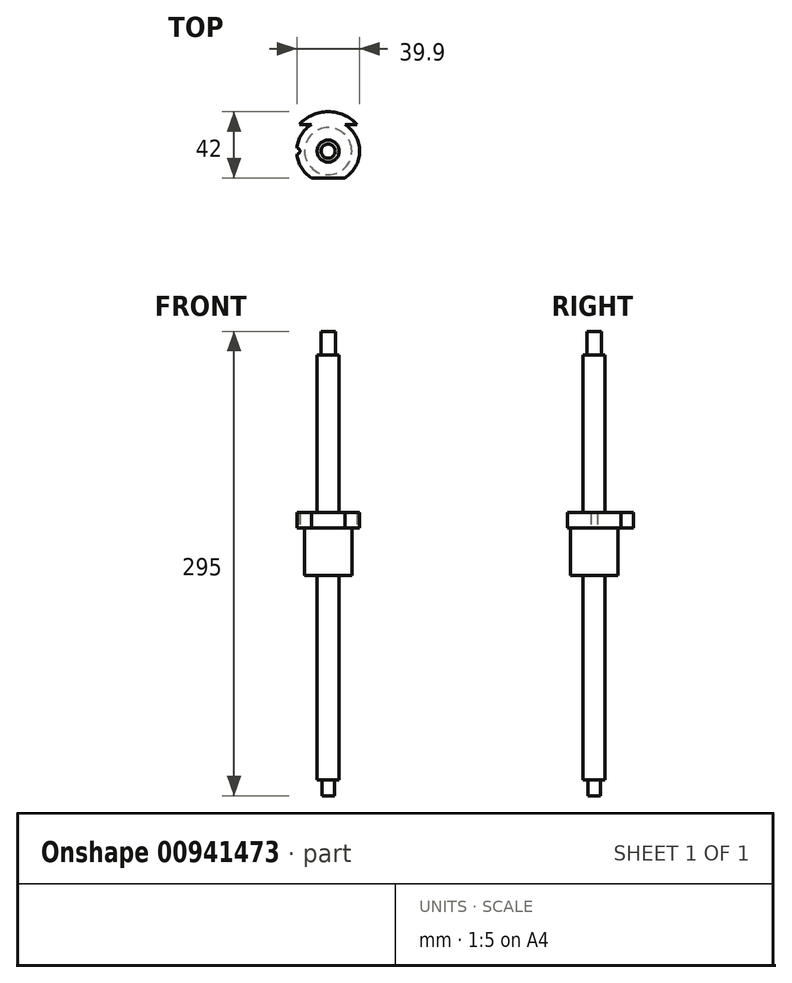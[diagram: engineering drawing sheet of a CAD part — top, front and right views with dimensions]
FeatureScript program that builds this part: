
annotation { "Feature Type Name" : "Feature", "Feature Type Description" : "" }
export const myFeature = defineFeature(function(context is Context, id is Id, definition is map)
    precondition{}
    {
        {
            var Q0;
            Q0=qCreatedBy(makeId("Top.planeOp"),FACE);
            var sketch = newSketch(context, id + "F0", { "sketchPlane" : qUnion([Q0])});
            skCircle(sketch, "E0", {"center": v(0, 0) * mm, "radius": 15 * mm});
            skSolve(sketch);
        }
        {
            var Q0;
            Q0=makeQuery(id+"F0.imprint","IMPRINT",FACE,{"disambiguationData":[TD([[makeQuery(id+"F0.imprint","IMPRINT",EDGE,{"derivedFrom":sQuery(id+"F0.wireOp",EDGE,"E0")}),1.0]])]});
            extrude(context, id + "F1", {"entities" : qUnion([Q0]), "depth" : 30 * mm, "offsetDistance" : 25 * mm});
        }
        {
            var Q0;
            Q0=makeQuery(id+"F1.opExtrude","CAP_FACE",FACE,{"disambiguationData":[OSD([sQuery(id+"F0.wireOp",EDGE,"E0")])],"isStart":false});
            var sketch = newSketch(context, id + "F2", { "sketchPlane" : qUnion([Q0])});
            skCircle(sketch, "E1", {"center": v(0, 0) * mm, "radius": 20 * mm});
            skCircle(sketch, "E2", {"center": v(0, 0) * mm, "radius": 25 * mm});
            skLineSegment(sketch, "E3.bottom", {"start": v(30.85, -17) * mm, "end": v(-30.85, -17) * mm});
            skLineSegment(sketch, "E3.top", {"start": v(30.85, 17) * mm, "end": v(-30.85, 17) * mm});
            skLineSegment(sketch, "E3.left", {"start": v(30.85, -17) * mm, "end": v(30.85, 17) * mm});
            skLineSegment(sketch, "E3.right", {"start": v(-30.85, -17) * mm, "end": v(-30.85, 17) * mm});
            skCircle(sketch, "E4", {"center": v(-20, 0) * mm, "radius": 2 * mm});
            skSolve(sketch);
        }
        {
            var Q0;
            Q0=makeQuery(id+"F2.imprint","IMPRINT",FACE,{"disambiguationData":[TD([[makeQuery(id+"F2.imprint","IMPRINT",EDGE,{"derivedFrom":makeQuery(id+"F1.opExtrude","CAP_EDGE",EDGE,{"disambiguationData":[OSD([sQuery(id+"F0.wireOp",EDGE,"E0")])],"isStart":false})}),-1.0]])]});
            var Q1;
            Q1=makeQuery(id+"F2.imprint","IMPRINT",FACE,{"disambiguationData":[TD([[makeQuery(id+"F2.imprint","IMPRINT",EDGE,{"derivedFrom":makeQuery(id+"F1.opExtrude","CAP_EDGE",EDGE,{"disambiguationData":[OSD([sQuery(id+"F0.wireOp",EDGE,"E0")])],"isStart":false})}),1.0]])]});
            var Q2;
            {var subQ0=sQuery(id+"F2.wireOp",EDGE,"E3.top");var subQ1=sQuery(id+"F2.wireOp",EDGE,"E1");var subQ2=makeQuery(id+"F2.imprint","INTERSECT",VERTEX,{"disambiguationData":[OD(0.0)],"derivedFrom":[subQ1,subQ0]});Q2=makeQuery(id+"F2.imprint","IMPRINT",FACE,{"disambiguationData":[TD([[makeQuery(id+"F2.imprint","IMPRINT",EDGE,{"disambiguationData":[TD([[subQ2,-1.0]])],"derivedFrom":subQ1}),1.0]])]});}
            var Q3;
            {var subQ0=sQuery(id+"F2.wireOp",EDGE,"E3.top");var subQ1=sQuery(id+"F2.wireOp",EDGE,"E1");var subQ2=makeQuery(id+"F2.imprint","INTERSECT",VERTEX,{"disambiguationData":[OD(1.0)],"derivedFrom":[subQ1,subQ0]});Q3=makeQuery(id+"F2.imprint","IMPRINT",FACE,{"disambiguationData":[TD([[makeQuery(id+"F2.imprint","IMPRINT",EDGE,{"disambiguationData":[TD([[subQ2,1.0]])],"derivedFrom":subQ1}),1.0]])]});}
            var Q4;
            {var subQ0=sQuery(id+"F2.wireOp",EDGE,"E3.top");var subQ5=sQuery(id+"F2.wireOp",EDGE,"E1");var subQ6=makeQuery(id+"F2.imprint","INTERSECT",VERTEX,{"disambiguationData":[OD(0.0)],"derivedFrom":[subQ5,subQ0]});Q4=makeQuery(id+"F2.imprint","IMPRINT",FACE,{"disambiguationData":[TD([[makeQuery(id+"F2.imprint","IMPRINT",EDGE,{"disambiguationData":[TD([[subQ6,-1.0]])],"derivedFrom":subQ5}),-1.0]])]});}
            var Q5;
            {var subQ0=sQuery(id+"F2.wireOp",EDGE,"E3.top");var subQ1=sQuery(id+"F2.wireOp",EDGE,"E1");var subQ2=makeQuery(id+"F2.imprint","INTERSECT",VERTEX,{"disambiguationData":[OD(1.0)],"derivedFrom":[subQ1,subQ0]});Q5=makeQuery(id+"F2.imprint","IMPRINT",FACE,{"disambiguationData":[TD([[makeQuery(id+"F2.imprint","IMPRINT",EDGE,{"disambiguationData":[TD([[subQ2,1.0]])],"derivedFrom":subQ1}),-1.0]])]});}
            var Q6;
            {var subQ0=sQuery(id+"F2.wireOp",EDGE,"E4");var subQ1=sQuery(id+"F2.wireOp",EDGE,"E1");var subQ2=makeQuery(id+"F2.imprint","INTERSECT",VERTEX,{"disambiguationData":[OD(0.0)],"derivedFrom":[subQ1,subQ0]});Q6=makeQuery(id+"F2.imprint","IMPRINT",FACE,{"disambiguationData":[TD([[makeQuery(id+"F2.imprint","IMPRINT",EDGE,{"disambiguationData":[TD([[subQ2,-1.0]])],"derivedFrom":subQ1}),1.0]])]});}
            var Q7;
            {var subQ0=sQuery(id+"F2.wireOp",EDGE,"E4");var subQ1=sQuery(id+"F2.wireOp",EDGE,"E1");var subQ2=makeQuery(id+"F2.imprint","INTERSECT",VERTEX,{"disambiguationData":[OD(0.0)],"derivedFrom":[subQ1,subQ0]});Q7=makeQuery(id+"F2.imprint","IMPRINT",FACE,{"disambiguationData":[TD([[makeQuery(id+"F2.imprint","IMPRINT",EDGE,{"disambiguationData":[TD([[subQ2,-1.0]])],"derivedFrom":subQ1}),-1.0]])]});}
            extrude(context, id + "F3", {"entities" : qUnion([Q0, Q1, Q2, Q3, Q4, Q5, Q6, Q7]), "operationType" : NewBodyOperationType.ADD, "depth" : 10 * mm, "offsetDistance" : 25 * mm});
        }
        {
            var Q0;
            {var subQ0=sQuery(id+"F2.wireOp",EDGE,"E4");var subQ1=sQuery(id+"F2.wireOp",EDGE,"E1");var subQ2=makeQuery(id+"F2.imprint","INTERSECT",VERTEX,{"disambiguationData":[OD(0.0)],"derivedFrom":[subQ1,subQ0]});Q0=makeQuery(id+"F2.imprint","IMPRINT",FACE,{"disambiguationData":[TD([[makeQuery(id+"F2.imprint","IMPRINT",EDGE,{"disambiguationData":[TD([[subQ2,-1.0]])],"derivedFrom":subQ1}),1.0]])]});}
            var Q1;
            {var subQ0=sQuery(id+"F2.wireOp",EDGE,"E4");var subQ1=sQuery(id+"F2.wireOp",EDGE,"E1");var subQ2=makeQuery(id+"F2.imprint","INTERSECT",VERTEX,{"disambiguationData":[OD(0.0)],"derivedFrom":[subQ1,subQ0]});Q1=makeQuery(id+"F2.imprint","IMPRINT",FACE,{"disambiguationData":[TD([[makeQuery(id+"F2.imprint","IMPRINT",EDGE,{"disambiguationData":[TD([[subQ2,-1.0]])],"derivedFrom":subQ1}),-1.0]])]});}
            extrude(context, id + "F4", {"entities" : qUnion([Q0, Q1]), "operationType" : NewBodyOperationType.REMOVE, "depth" : 25 * mm, "offsetDistance" : 25 * mm});
        }
        {
            var Q0;
            Q0=qCreatedBy(makeId("Right.planeOp"),FACE);
            var sketch = newSketch(context, id + "F5", { "sketchPlane" : qUnion([Q0])});
            skLineSegment(sketch, "E5", {"start": v(0, 0) * mm, "end": v(0, -16.32) * mm, "construction": true});
            skSolve(sketch);
        }
        {
            var Q0;
            Q0=makeQuery(id+"F1.opExtrude","CAP_FACE",FACE,{"disambiguationData":[OSD([sQuery(id+"F0.wireOp",EDGE,"E0")])],"isStart":true});
            var sketch = newSketch(context, id + "F6", { "sketchPlane" : qUnion([Q0])});
            skCircle(sketch, "E6", {"center": v(0, 0) * mm, "radius": 7 * mm});
            skSolve(sketch);
        }
        {
            var Q0;
            Q0=makeQuery(id+"F6.imprint","IMPRINT",FACE,{"disambiguationData":[TD([[makeQuery(id+"F6.imprint","IMPRINT",EDGE,{"derivedFrom":sQuery(id+"F6.wireOp",EDGE,"E6")}),1.0]])]});
            extrude(context, id + "F7", {"entities" : qUnion([Q0]), "operationType" : NewBodyOperationType.ADD, "depth" : 130 * mm, "offsetDistance" : 25 * mm, "hasSecondDirection" : true, "secondDirectionOppositeDirection" : true, "secondDirectionDepth" : 140 * mm});
        }
        {
            var Q0;
            Q0=makeQuery(id+"F7.opExtrude","CAP_FACE",FACE,{"disambiguationData":[OSD([sQuery(id+"F6.wireOp",EDGE,"E6")])],"isStart":false});
            var sketch = newSketch(context, id + "F8", { "sketchPlane" : qUnion([Q0])});
            skCircle(sketch, "E7", {"center": v(0, 0) * mm, "radius": 4 * mm});
            skSolve(sketch);
        }
        {
            var Q0;
            Q0=makeQuery(id+"F8.imprint","IMPRINT",FACE,{"disambiguationData":[TD([[makeQuery(id+"F8.imprint","IMPRINT",EDGE,{"derivedFrom":sQuery(id+"F8.wireOp",EDGE,"E7")}),1.0]])]});
            extrude(context, id + "F9", {"entities" : qUnion([Q0]), "operationType" : NewBodyOperationType.ADD, "depth" : 10 * mm, "offsetDistance" : 25 * mm});
        }
        {
            var Q0;
            Q0=makeQuery(id+"F7.opExtrude","CAP_FACE",FACE,{"disambiguationData":[OSD([sQuery(id+"F6.wireOp",EDGE,"E6")])],"isStart":true});
            var sketch = newSketch(context, id + "F10", { "sketchPlane" : qUnion([Q0])});
            skCircle(sketch, "E8", {"center": v(0, 0) * mm, "radius": 4.5 * mm});
            skSolve(sketch);
        }
        {
            var Q0;
            Q0=makeQuery(id+"F10.imprint","IMPRINT",FACE,{"disambiguationData":[TD([[makeQuery(id+"F10.imprint","IMPRINT",EDGE,{"derivedFrom":sQuery(id+"F10.wireOp",EDGE,"E8")}),1.0]])]});
            extrude(context, id + "F11", {"entities" : qUnion([Q0]), "operationType" : NewBodyOperationType.ADD, "depth" : 15 * mm, "offsetDistance" : 25 * mm});
        }
    });
